# Revit family: Domotics-SerieCivili-GEWISS-27COMBI22-IP66_CONTENITORI_3PULSANTI_D22
name_source: partatom
category: Apparecchi elettrici
revit_build: Autodesk Revit 2016 (Build: 20161004_0715(x64)
units: mm (PartAtom-declared; Revit-internal decimal feet)

## family parameters
Condiviso = No
Host = Muro
Mantenere orientamento annotazione = No
Punto di calcolo locali = No
Quota connettore circolare = Usa diametro
Sempre verticale = Sì
Taglio con vuoti quando caricato = No
Tipo di parte = Normale

## types (1)
- Domotics-SerieCivili-GEWISS-27COMBI22-IP66_CONTENITORI_3PULSANTI_D22
    Altezza = 171 mm  [stored 0.561024 ft]
    Catalogo = DOMOTICS
    Catalogo Serie = 27COMBI
    Classe isolamento = II
    Codice EAN = 8011564055599
    Codice Electrocod = 0212
    Colore = Grigio RAL 7035
    Contatti = 1 NA-1 NC
    Coppia serraggio viti = 0,8NM
    Descrizione = CONTENITORE 3POS.PULSANTE MAR./ARR.+SEG.
    Dim. esterne BxHxP (mm) = 66x171x65
    Glow Wire Test = 650°C
    Grado di protezione = IP66
    IDF = 702eae9a-7075-476e-8d8e-c77066508fad
    IDT = eb43bfa2-97ff-42a8-b7a2-23da41b5a658
    Immagine tipo = GW27204.jpg
    Larghezza = 82 mm  [stored 0.269029 ft]
    Modello = GW27204
    N. posti = 3
    Norma di riferimento = EN 60947-1 - EN 60947-5-1
    Norma di riferimento: = EN 60947-1 - EN 60947-5-1
    Operatori Ã˜ 22 = Marcia, arresto, segnalazione
    Produttore = GEWISS S.p.A.
    Profondità = 65 mm
    Pulsante_1 = Pulsante marcia -verde
    Pulsante_2 = Pulsante arresto - rosso
    Pulsante_3 = Pulsante segnalazione - grigio
    SEO = Contenitore
    Scheda Tecnica = https://www.gewiss.com
    Temperatura di installazione = -25 +60 °C
    Termopressione con biglia = 70 °C
    Tipo sfondabili = Asportabili con utensile
    URL = https://www.gewiss.com
    Versione file RFA = 18.0
    Viti coperchio = Acciaio inox

note: [stored X ft] marks values corroborated as IEEE doubles in the binary element streams (Revit-internal decimal feet)
